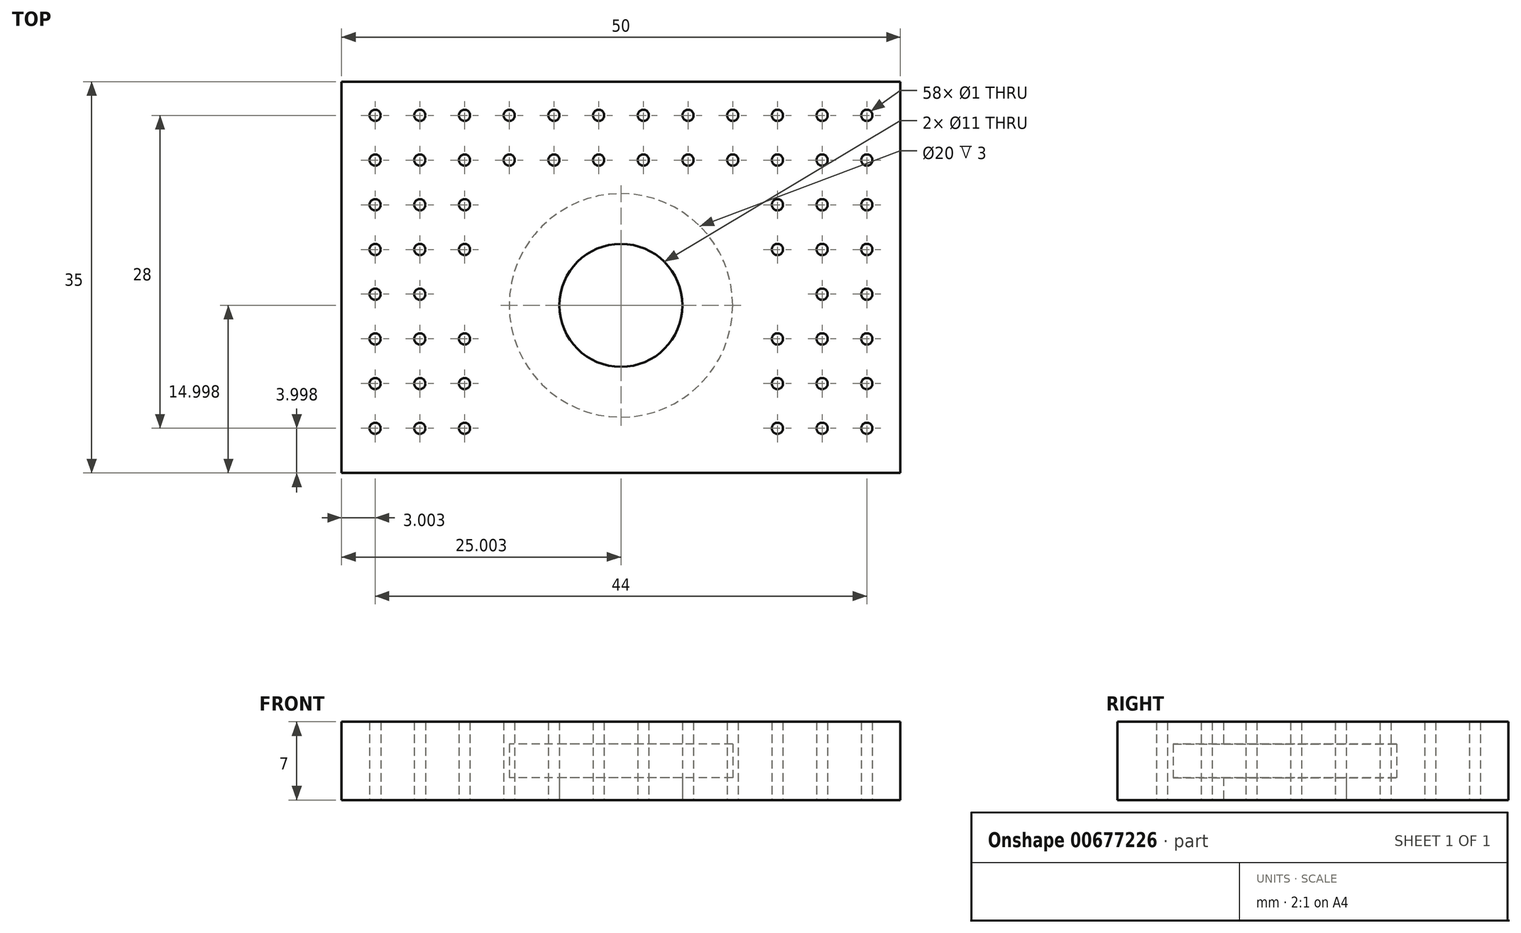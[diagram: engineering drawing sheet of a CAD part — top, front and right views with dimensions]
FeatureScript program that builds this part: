
annotation { "Feature Type Name" : "Feature", "Feature Type Description" : "" }
export const myFeature = defineFeature(function(context is Context, id is Id, definition is map)
    precondition{}
    {
        {
            var Q0;
            Q0=qCreatedBy(makeId("Top.planeOp"),FACE);
            var sketch = newSketch(context, id + "F0", { "sketchPlane" : qUnion([Q0])});
            skLineSegment(sketch, "E0.bottom", {"start": v(-33.44, 20.69) * mm, "end": v(16.56, 20.69) * mm});
            skLineSegment(sketch, "E0.top", {"start": v(-33.44, -14.31) * mm, "end": v(16.56, -14.31) * mm});
            skLineSegment(sketch, "E0.left", {"start": v(-33.44, 20.69) * mm, "end": v(-33.44, -14.31) * mm});
            skLineSegment(sketch, "E0.right", {"start": v(16.56, 20.69) * mm, "end": v(16.56, -14.31) * mm});
            skCircle(sketch, "E1", {"center": v(-8.44, 0.69) * mm, "radius": 5.5 * mm});
            skCircle(sketch, "E2", {"center": v(-8.44, 0.69) * mm, "radius": 10 * mm});
            skCircle(sketch, "E3", {"center": v(-30.44, 17.69) * mm, "radius": 0.5 * mm});
            skCircle(sketch, "E4.1.0.0", {"center": v(-26.44, 17.69) * mm, "radius": 0.5 * mm});
            skCircle(sketch, "E4.2.0.0", {"center": v(-22.44, 17.69) * mm, "radius": 0.5 * mm});
            skCircle(sketch, "E4.3.0.0", {"center": v(-18.44, 17.69) * mm, "radius": 0.5 * mm});
            skCircle(sketch, "E4.4.0.0", {"center": v(-14.44, 17.69) * mm, "radius": 0.5 * mm});
            skCircle(sketch, "E4.5.0.0", {"center": v(-10.44, 17.69) * mm, "radius": 0.5 * mm});
            skCircle(sketch, "E4.6.0.0", {"center": v(-6.44, 17.69) * mm, "radius": 0.5 * mm});
            skCircle(sketch, "E4.7.0.0", {"center": v(-2.44, 17.69) * mm, "radius": 0.5 * mm});
            skCircle(sketch, "E4.8.0.0", {"center": v(1.56, 17.69) * mm, "radius": 0.5 * mm});
            skCircle(sketch, "E4.9.0.0", {"center": v(5.56, 17.69) * mm, "radius": 0.5 * mm});
            skCircle(sketch, "E4.10.0.0", {"center": v(9.56, 17.69) * mm, "radius": 0.5 * mm});
            skLineSegment(sketch, "E4.direction1", {"start": v(-30.44, 17.69) * mm, "end": v(-26.44, 17.69) * mm, "construction": true});
            skCircle(sketch, "E5.0.11.0", {"center": v(13.56, 17.69) * mm, "radius": 0.5 * mm});
            skCircle(sketch, "E6.1.0.0", {"center": v(1.56, 13.69) * mm, "radius": 0.5 * mm});
            skCircle(sketch, "E6.1.0.1", {"center": v(5.56, 13.69) * mm, "radius": 0.5 * mm});
            skLineSegment(sketch, "E6.1.0.2", {"start": v(-30.44, 13.69) * mm, "end": v(-26.44, 13.69) * mm, "construction": true});
            skCircle(sketch, "E6.1.0.3", {"center": v(-2.44, 13.69) * mm, "radius": 0.5 * mm});
            skCircle(sketch, "E6.1.0.4", {"center": v(-30.44, 13.69) * mm, "radius": 0.5 * mm});
            skCircle(sketch, "E6.1.0.5", {"center": v(-26.44, 13.69) * mm, "radius": 0.5 * mm});
            skCircle(sketch, "E6.1.0.6", {"center": v(-22.44, 13.69) * mm, "radius": 0.5 * mm});
            skCircle(sketch, "E6.1.0.7", {"center": v(-18.44, 13.69) * mm, "radius": 0.5 * mm});
            skCircle(sketch, "E6.1.0.8", {"center": v(-14.44, 13.69) * mm, "radius": 0.5 * mm});
            skCircle(sketch, "E6.1.0.9", {"center": v(-10.44, 13.69) * mm, "radius": 0.5 * mm});
            skCircle(sketch, "E6.1.0.10", {"center": v(-6.44, 13.69) * mm, "radius": 0.5 * mm});
            skCircle(sketch, "E6.1.0.11", {"center": v(13.56, 13.69) * mm, "radius": 0.5 * mm});
            skCircle(sketch, "E6.1.0.12", {"center": v(9.56, 13.69) * mm, "radius": 0.5 * mm});
            skCircle(sketch, "E6.2.0.1", {"center": v(5.56, 9.69) * mm, "radius": 0.5 * mm});
            skLineSegment(sketch, "E6.2.0.2", {"start": v(-30.44, 9.69) * mm, "end": v(-26.44, 9.69) * mm, "construction": true});
            skCircle(sketch, "E6.2.0.4", {"center": v(-30.44, 9.69) * mm, "radius": 0.5 * mm});
            skCircle(sketch, "E6.2.0.5", {"center": v(-26.44, 9.69) * mm, "radius": 0.5 * mm});
            skCircle(sketch, "E6.2.0.6", {"center": v(-22.44, 9.69) * mm, "radius": 0.5 * mm});
            skCircle(sketch, "E6.2.0.11", {"center": v(13.56, 9.69) * mm, "radius": 0.5 * mm});
            skCircle(sketch, "E6.2.0.12", {"center": v(9.56, 9.69) * mm, "radius": 0.5 * mm});
            skCircle(sketch, "E6.3.0.1", {"center": v(5.56, 5.69) * mm, "radius": 0.5 * mm});
            skLineSegment(sketch, "E6.3.0.2", {"start": v(-30.44, 5.69) * mm, "end": v(-26.44, 5.69) * mm, "construction": true});
            skCircle(sketch, "E6.3.0.4", {"center": v(-30.44, 5.69) * mm, "radius": 0.5 * mm});
            skCircle(sketch, "E6.3.0.5", {"center": v(-26.44, 5.69) * mm, "radius": 0.5 * mm});
            skCircle(sketch, "E6.3.0.6", {"center": v(-22.44, 5.69) * mm, "radius": 0.5 * mm});
            skCircle(sketch, "E6.3.0.11", {"center": v(13.56, 5.69) * mm, "radius": 0.5 * mm});
            skCircle(sketch, "E6.3.0.12", {"center": v(9.56, 5.69) * mm, "radius": 0.5 * mm});
            skLineSegment(sketch, "E6.4.0.2", {"start": v(-30.44, 1.69) * mm, "end": v(-26.44, 1.69) * mm, "construction": true});
            skCircle(sketch, "E6.4.0.4", {"center": v(-30.44, 1.69) * mm, "radius": 0.5 * mm});
            skCircle(sketch, "E6.4.0.5", {"center": v(-26.44, 1.69) * mm, "radius": 0.5 * mm});
            skCircle(sketch, "E6.4.0.11", {"center": v(13.56, 1.69) * mm, "radius": 0.5 * mm});
            skCircle(sketch, "E6.4.0.12", {"center": v(9.56, 1.69) * mm, "radius": 0.5 * mm});
            skCircle(sketch, "E6.5.0.1", {"center": v(5.56, -2.31) * mm, "radius": 0.5 * mm});
            skLineSegment(sketch, "E6.5.0.2", {"start": v(-30.44, -2.31) * mm, "end": v(-26.44, -2.31) * mm, "construction": true});
            skCircle(sketch, "E6.5.0.4", {"center": v(-30.44, -2.31) * mm, "radius": 0.5 * mm});
            skCircle(sketch, "E6.5.0.5", {"center": v(-26.44, -2.31) * mm, "radius": 0.5 * mm});
            skCircle(sketch, "E6.5.0.6", {"center": v(-22.44, -2.31) * mm, "radius": 0.5 * mm});
            skCircle(sketch, "E6.5.0.11", {"center": v(13.56, -2.31) * mm, "radius": 0.5 * mm});
            skCircle(sketch, "E6.5.0.12", {"center": v(9.56, -2.31) * mm, "radius": 0.5 * mm});
            skCircle(sketch, "E6.6.0.1", {"center": v(5.56, -6.31) * mm, "radius": 0.5 * mm});
            skLineSegment(sketch, "E6.6.0.2", {"start": v(-30.44, -6.31) * mm, "end": v(-26.44, -6.31) * mm, "construction": true});
            skCircle(sketch, "E6.6.0.4", {"center": v(-30.44, -6.31) * mm, "radius": 0.5 * mm});
            skCircle(sketch, "E6.6.0.5", {"center": v(-26.44, -6.31) * mm, "radius": 0.5 * mm});
            skCircle(sketch, "E6.6.0.6", {"center": v(-22.44, -6.31) * mm, "radius": 0.5 * mm});
            skCircle(sketch, "E6.6.0.11", {"center": v(13.56, -6.31) * mm, "radius": 0.5 * mm});
            skCircle(sketch, "E6.6.0.12", {"center": v(9.56, -6.31) * mm, "radius": 0.5 * mm});
            skCircle(sketch, "E6.7.0.1", {"center": v(5.56, -10.31) * mm, "radius": 0.5 * mm});
            skLineSegment(sketch, "E6.7.0.2", {"start": v(-30.44, -10.31) * mm, "end": v(-26.44, -10.31) * mm, "construction": true});
            skCircle(sketch, "E6.7.0.4", {"center": v(-30.44, -10.31) * mm, "radius": 0.5 * mm});
            skCircle(sketch, "E6.7.0.5", {"center": v(-26.44, -10.31) * mm, "radius": 0.5 * mm});
            skCircle(sketch, "E6.7.0.6", {"center": v(-22.44, -10.31) * mm, "radius": 0.5 * mm});
            skCircle(sketch, "E6.7.0.11", {"center": v(13.56, -10.31) * mm, "radius": 0.5 * mm});
            skCircle(sketch, "E6.7.0.12", {"center": v(9.56, -10.31) * mm, "radius": 0.5 * mm});
            skLineSegment(sketch, "E6.direction1", {"start": v(-30.44, 17.69) * mm, "end": v(-30.44, 13.69) * mm, "construction": true});
            skSolve(sketch);
        }
        {
            var Q0;
            Q0=makeQuery(id+"F0.imprint","IMPRINT",FACE,{"disambiguationData":[TD([[makeQuery(id+"F0.imprint","IMPRINT",EDGE,{"derivedFrom":sQuery(id+"F0.wireOp",EDGE,"E0.bottom")}),-1.0]])]});
            var Q1;
            Q1=makeQuery(id+"F0.imprint","IMPRINT",FACE,{"disambiguationData":[TD([[makeQuery(id+"F0.imprint","IMPRINT",EDGE,{"derivedFrom":sQuery(id+"F0.wireOp",EDGE,"E1")}),-1.0]])]});
            extrude(context, id + "F1", {"entities" : qUnion([Q0, Q1]), "depth" : 7 * mm, "offsetDistance" : 25 * mm});
        }
        {
            var Q0;
            Q0=makeQuery(id+"F0.imprint","IMPRINT",FACE,{"disambiguationData":[TD([[makeQuery(id+"F0.imprint","IMPRINT",EDGE,{"derivedFrom":sQuery(id+"F0.wireOp",EDGE,"E1")}),-1.0]])]});
            extrude(context, id + "F2", {"entities" : qUnion([Q0]), "depth" : 5 * mm, "offsetDistance" : 25 * mm, "hasSecondDirection" : true, "secondDirectionOppositeDirection" : true, "secondDirectionDepth" : -2 * mm});
        }
        {
            var Q0;
            Q0=makeQuery(id+"F2.opExtrude","SWEPT_BODY",BODY,{"disambiguationData":[OSD([sQuery(id+"F0.wireOp",EDGE,"E1"),sQuery(id+"F0.wireOp",EDGE,"E2")])]});
            var Q1;
            Q1=makeQuery(id+"F1.opExtrude","SWEPT_BODY",BODY,{"disambiguationData":[OSD([sQuery(id+"F0.wireOp",EDGE,"E0.bottom"),sQuery(id+"F0.wireOp",EDGE,"E0.top"),sQuery(id+"F0.wireOp",EDGE,"E0.left"),sQuery(id+"F0.wireOp",EDGE,"E0.right"),sQuery(id+"F0.wireOp",EDGE,"E1"),sQuery(id+"F0.wireOp",EDGE,"E3"),sQuery(id+"F0.wireOp",EDGE,"E4.1.0.0"),sQuery(id+"F0.wireOp",EDGE,"E4.2.0.0"),sQuery(id+"F0.wireOp",EDGE,"E4.3.0.0"),sQuery(id+"F0.wireOp",EDGE,"E4.4.0.0"),sQuery(id+"F0.wireOp",EDGE,"E4.5.0.0"),sQuery(id+"F0.wireOp",EDGE,"E4.6.0.0"),sQuery(id+"F0.wireOp",EDGE,"E4.7.0.0"),sQuery(id+"F0.wireOp",EDGE,"E4.8.0.0"),sQuery(id+"F0.wireOp",EDGE,"E4.9.0.0"),sQuery(id+"F0.wireOp",EDGE,"E4.10.0.0"),sQuery(id+"F0.wireOp",EDGE,"E5.0.11.0"),sQuery(id+"F0.wireOp",EDGE,"E6.1.0.0"),sQuery(id+"F0.wireOp",EDGE,"E6.1.0.1"),sQuery(id+"F0.wireOp",EDGE,"E6.1.0.3"),sQuery(id+"F0.wireOp",EDGE,"E6.1.0.4"),sQuery(id+"F0.wireOp",EDGE,"E6.1.0.5"),sQuery(id+"F0.wireOp",EDGE,"E6.1.0.6"),sQuery(id+"F0.wireOp",EDGE,"E6.1.0.7"),sQuery(id+"F0.wireOp",EDGE,"E6.1.0.8"),sQuery(id+"F0.wireOp",EDGE,"E6.1.0.9"),sQuery(id+"F0.wireOp",EDGE,"E6.1.0.10"),sQuery(id+"F0.wireOp",EDGE,"E6.1.0.11"),sQuery(id+"F0.wireOp",EDGE,"E6.1.0.12"),sQuery(id+"F0.wireOp",EDGE,"E6.2.0.1"),sQuery(id+"F0.wireOp",EDGE,"E6.2.0.4"),sQuery(id+"F0.wireOp",EDGE,"E6.2.0.5"),sQuery(id+"F0.wireOp",EDGE,"E6.2.0.6"),sQuery(id+"F0.wireOp",EDGE,"E6.2.0.11"),sQuery(id+"F0.wireOp",EDGE,"E6.2.0.12"),sQuery(id+"F0.wireOp",EDGE,"E6.3.0.1"),sQuery(id+"F0.wireOp",EDGE,"E6.3.0.4"),sQuery(id+"F0.wireOp",EDGE,"E6.3.0.5"),sQuery(id+"F0.wireOp",EDGE,"E6.3.0.6"),sQuery(id+"F0.wireOp",EDGE,"E6.3.0.11"),sQuery(id+"F0.wireOp",EDGE,"E6.3.0.12"),sQuery(id+"F0.wireOp",EDGE,"E6.4.0.4"),sQuery(id+"F0.wireOp",EDGE,"E6.4.0.5"),sQuery(id+"F0.wireOp",EDGE,"E6.4.0.11"),sQuery(id+"F0.wireOp",EDGE,"E6.4.0.12"),sQuery(id+"F0.wireOp",EDGE,"E6.5.0.1"),sQuery(id+"F0.wireOp",EDGE,"E6.5.0.4"),sQuery(id+"F0.wireOp",EDGE,"E6.5.0.5"),sQuery(id+"F0.wireOp",EDGE,"E6.5.0.6"),sQuery(id+"F0.wireOp",EDGE,"E6.5.0.11"),sQuery(id+"F0.wireOp",EDGE,"E6.5.0.12"),sQuery(id+"F0.wireOp",EDGE,"E6.6.0.1"),sQuery(id+"F0.wireOp",EDGE,"E6.6.0.4"),sQuery(id+"F0.wireOp",EDGE,"E6.6.0.5"),sQuery(id+"F0.wireOp",EDGE,"E6.6.0.6"),sQuery(id+"F0.wireOp",EDGE,"E6.6.0.11"),sQuery(id+"F0.wireOp",EDGE,"E6.6.0.12"),sQuery(id+"F0.wireOp",EDGE,"E6.7.0.1"),sQuery(id+"F0.wireOp",EDGE,"E6.7.0.4"),sQuery(id+"F0.wireOp",EDGE,"E6.7.0.5"),sQuery(id+"F0.wireOp",EDGE,"E6.7.0.6"),sQuery(id+"F0.wireOp",EDGE,"E6.7.0.11"),sQuery(id+"F0.wireOp",EDGE,"E6.7.0.12")])]});
            booleanBodies(context, id + "F3", {"operationType" : BooleanOperationType.SUBTRACTION, "tools" : qUnion([Q0]), "targets" : qUnion([Q1])});
        }
    });
